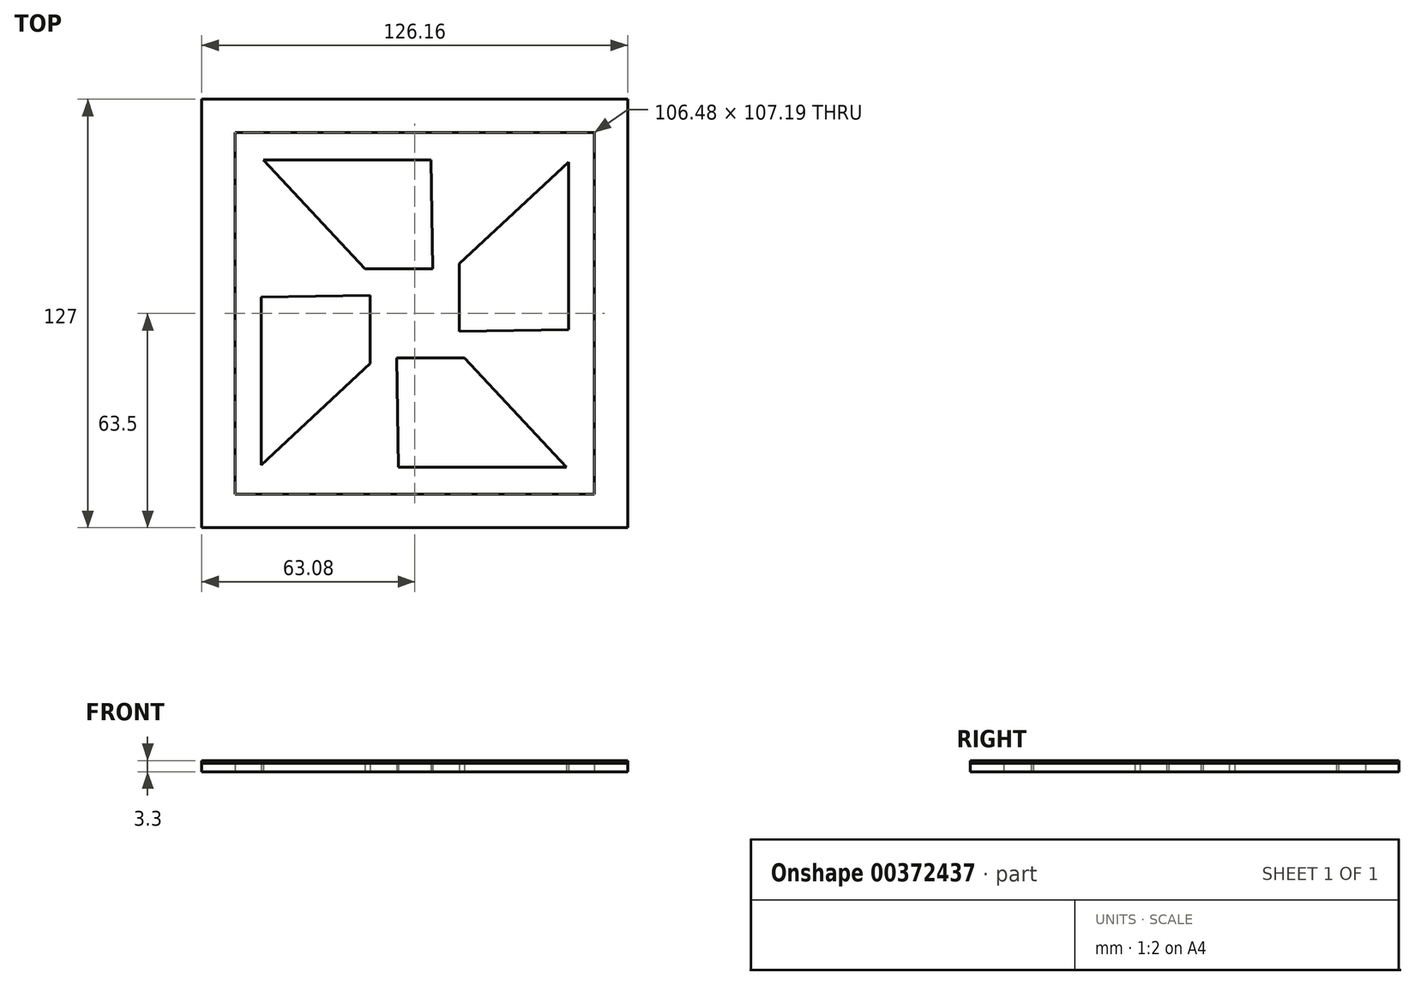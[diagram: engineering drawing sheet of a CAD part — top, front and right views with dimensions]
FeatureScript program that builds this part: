
annotation { "Feature Type Name" : "Feature", "Feature Type Description" : "" }
export const myFeature = defineFeature(function(context is Context, id is Id, definition is map)
    precondition{}
    {
        {
            var Q0;
            Q0=qCreatedBy(makeId("Top.planeOp"),FACE);
            var sketch = newSketch(context, id + "F0", { "sketchPlane" : qUnion([Q0])});
            skLineSegment(sketch, "E0.bottom", {"start": v(0, 0) * mm, "end": v(126.16, 0) * mm});
            skLineSegment(sketch, "E0.top", {"start": v(0, 127) * mm, "end": v(126.16, 127) * mm});
            skLineSegment(sketch, "E0.left", {"start": v(0, 0) * mm, "end": v(0, 127) * mm});
            skLineSegment(sketch, "E0.right", {"start": v(126.16, 0) * mm, "end": v(126.16, 127) * mm});
            skLineSegment(sketch, "E1", {"start": v(68.44, 76.71) * mm, "end": v(48.31, 76.71) * mm});
            skLineSegment(sketch, "E2", {"start": v(48.31, 76.71) * mm, "end": v(18.18, 109.04) * mm});
            skLineSegment(sketch, "E3", {"start": v(18.18, 109.04) * mm, "end": v(67.89, 109.04) * mm});
            skLineSegment(sketch, "E4", {"start": v(67.89, 109.04) * mm, "end": v(68.44, 76.71) * mm});
            skLineSegment(sketch, "E5", {"start": v(0, 127) * mm, "end": v(126.16, 0) * mm, "construction": true});
            skPoint(sketch, "E6", {"position": v(63.08, 63.5) * mm});
            skLineSegment(sketch, "E7.1.0", {"start": v(17.54, 68.3) * mm, "end": v(49.87, 68.86) * mm});
            skLineSegment(sketch, "E7.1.1", {"start": v(17.54, 18.6) * mm, "end": v(17.54, 68.3) * mm});
            skLineSegment(sketch, "E7.1.2", {"start": v(49.87, 48.73) * mm, "end": v(17.54, 18.6) * mm});
            skLineSegment(sketch, "E7.1.3", {"start": v(49.87, 68.86) * mm, "end": v(49.87, 48.73) * mm});
            skLineSegment(sketch, "E7.2.0", {"start": v(58.27, 17.96) * mm, "end": v(57.72, 50.29) * mm});
            skLineSegment(sketch, "E7.2.1", {"start": v(107.97, 17.96) * mm, "end": v(58.27, 17.96) * mm});
            skLineSegment(sketch, "E7.2.2", {"start": v(77.85, 50.29) * mm, "end": v(107.97, 17.96) * mm});
            skLineSegment(sketch, "E7.2.3", {"start": v(57.72, 50.29) * mm, "end": v(77.85, 50.29) * mm});
            skLineSegment(sketch, "E7.anchor1", {"start": v(63.08, 63.5) * mm, "end": v(48.31, 76.71) * mm, "construction": true});
            skLineSegment(sketch, "E7.anchor2", {"start": v(63.08, 63.5) * mm, "end": v(76.3, 78.27) * mm, "construction": true});
            skLineSegment(sketch, "E8.3.3.0", {"start": v(108.62, 108.4) * mm, "end": v(108.62, 58.7) * mm});
            skLineSegment(sketch, "E8.6.3.0", {"start": v(76.3, 78.27) * mm, "end": v(108.62, 108.4) * mm});
            skLineSegment(sketch, "E8.7.3.0", {"start": v(108.62, 58.7) * mm, "end": v(76.3, 58.14) * mm});
            skLineSegment(sketch, "E8.9.3.0", {"start": v(76.3, 58.14) * mm, "end": v(76.3, 78.27) * mm});
            skLineSegment(sketch, "E9.bottom", {"start": v(9.84, 117.1) * mm, "end": v(116.32, 117.1) * mm});
            skLineSegment(sketch, "E9.top", {"start": v(9.84, 9.9) * mm, "end": v(116.32, 9.9) * mm});
            skLineSegment(sketch, "E9.left", {"start": v(9.84, 117.1) * mm, "end": v(9.84, 9.9) * mm});
            skLineSegment(sketch, "E9.right", {"start": v(116.32, 117.1) * mm, "end": v(116.32, 9.9) * mm});
            skPoint(sketch, "E10", {"position": v(63.08, 117.1) * mm});
            skPoint(sketch, "E11", {"position": v(116.32, 63.5) * mm});
            skPoint(sketch, "E12", {"position": v(63.08, 9.9) * mm});
            skPoint(sketch, "E13", {"position": v(9.84, 63.5) * mm});
            skSolve(sketch);
        }
        {
            var Q0;
            Q0=makeQuery(id+"F0.imprint","IMPRINT",FACE,{"disambiguationData":[TD([[makeQuery(id+"F0.imprint","IMPRINT",EDGE,{"derivedFrom":sQuery(id+"F0.wireOp",EDGE,"E1")}),-1.0]])]});
            var Q1;
            Q1=makeQuery(id+"F0.imprint","IMPRINT",FACE,{"disambiguationData":[TD([[makeQuery(id+"F0.imprint","IMPRINT",EDGE,{"derivedFrom":sQuery(id+"F0.wireOp",EDGE,"E8.3.3.0")}),-1.0]])]});
            var Q2;
            Q2=makeQuery(id+"F0.imprint","IMPRINT",FACE,{"disambiguationData":[TD([[makeQuery(id+"F0.imprint","IMPRINT",EDGE,{"derivedFrom":sQuery(id+"F0.wireOp",EDGE,"E7.2.0")}),-1.0]])]});
            var Q3;
            Q3=makeQuery(id+"F0.imprint","IMPRINT",FACE,{"disambiguationData":[TD([[makeQuery(id+"F0.imprint","IMPRINT",EDGE,{"derivedFrom":sQuery(id+"F0.wireOp",EDGE,"E7.1.0")}),-1.0]])]});
            var Q4;
            Q4=makeQuery(id+"F0.imprint","IMPRINT",FACE,{"disambiguationData":[TD([[makeQuery(id+"F0.imprint","IMPRINT",EDGE,{"derivedFrom":sQuery(id+"F0.wireOp",EDGE,"E0.bottom")}),1.0]])]});
            extrude(context, id + "F1", {"entities" : qUnion([Q0, Q1, Q2, Q3, Q4]), "depth" : 3.3 * mm});
        }
        {
            var Q0;
            Q0=qCreatedBy(makeId("Top.planeOp"),FACE);
            var sketch = newSketch(context, id + "F2", { "sketchPlane" : qUnion([Q0])});
            skLineSegment(sketch, "E14.bottom", {"start": v(0, 0) * mm, "end": v(126.16, 0) * mm});
            skLineSegment(sketch, "E14.top", {"start": v(0, 127) * mm, "end": v(126.16, 127) * mm});
            skLineSegment(sketch, "E14.left", {"start": v(0, 0) * mm, "end": v(0, 127) * mm});
            skLineSegment(sketch, "E14.right", {"start": v(126.16, 0) * mm, "end": v(126.16, 127) * mm});
            skSolve(sketch);
        }
        {
            var Q0;
            Q0 = qSketchRegion(id + "F2", true);
            extrude(context, id + "F3", {"entities" : qUnion([Q0]), "depth" : 2.54 * mm});
        }
    });
